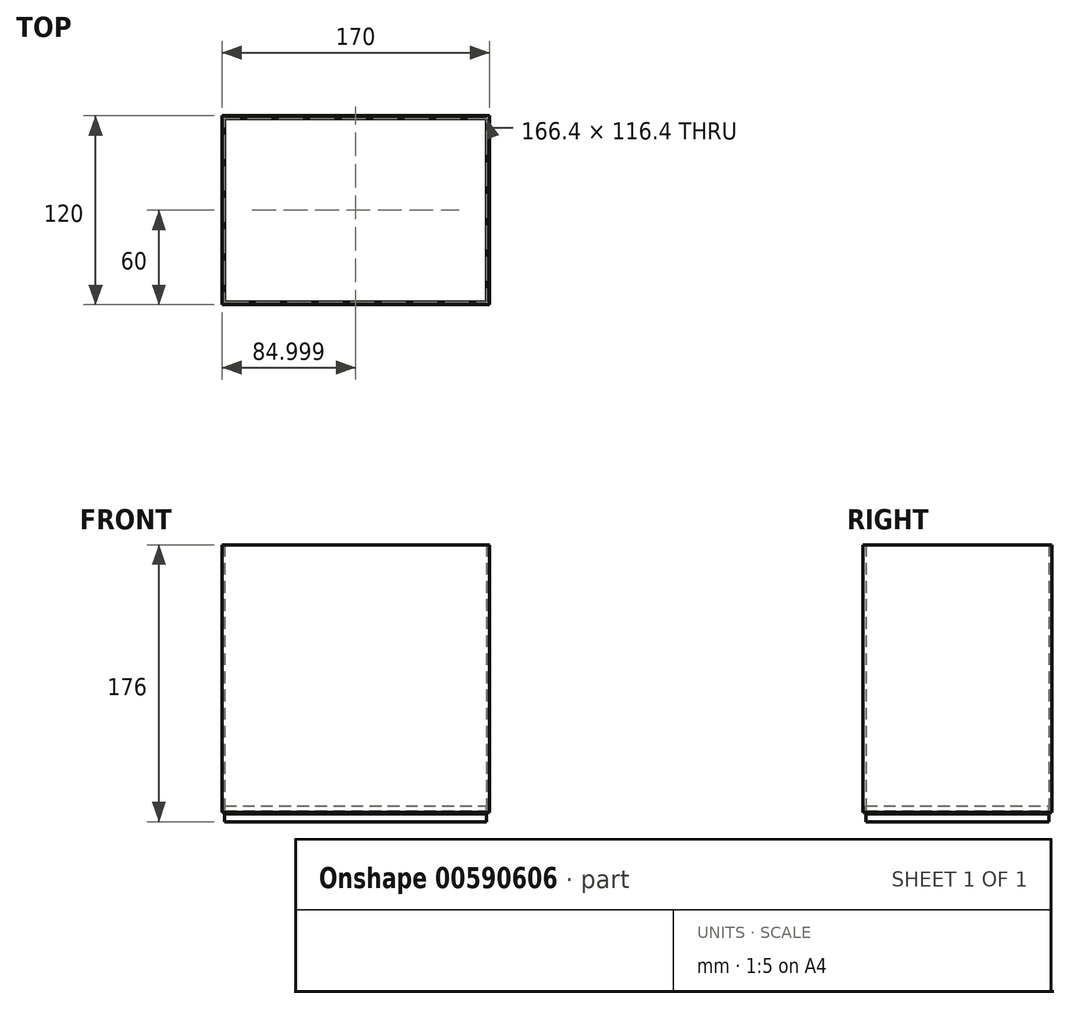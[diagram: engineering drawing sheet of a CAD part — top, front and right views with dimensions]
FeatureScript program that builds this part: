
annotation { "Feature Type Name" : "Feature", "Feature Type Description" : "" }
export const myFeature = defineFeature(function(context is Context, id is Id, definition is map)
    precondition{}
    {
        {
            var Q0;
            Q0=qCreatedBy(makeId("Top.planeOp"),FACE);
            var sketch = newSketch(context, id + "F0", { "sketchPlane" : qUnion([Q0])});
            skLineSegment(sketch, "E0.bottom", {"start": v(-78.22, 181.55) * mm, "end": v(91.78, 181.55) * mm});
            skLineSegment(sketch, "E0.top", {"start": v(-78.22, 61.55) * mm, "end": v(91.78, 61.55) * mm});
            skLineSegment(sketch, "E0.left", {"start": v(-78.22, 181.55) * mm, "end": v(-78.22, 61.55) * mm});
            skLineSegment(sketch, "E0.right", {"start": v(91.78, 181.55) * mm, "end": v(91.78, 61.55) * mm});
            skLineSegment(sketch, "E1.bottom", {"start": v(-76.42, 179.75) * mm, "end": v(89.98, 179.75) * mm});
            skLineSegment(sketch, "E1.top", {"start": v(-76.42, 63.35) * mm, "end": v(89.98, 63.35) * mm});
            skLineSegment(sketch, "E1.left", {"start": v(-76.42, 179.75) * mm, "end": v(-76.42, 63.35) * mm});
            skLineSegment(sketch, "E1.right", {"start": v(89.98, 179.75) * mm, "end": v(89.98, 63.35) * mm});
            skLineSegment(sketch, "E2.bottom", {"start": v(-76.42, -118.2) * mm, "end": v(93.58, -118.2) * mm});
            skLineSegment(sketch, "E2.top", {"start": v(-76.42, 1.8) * mm, "end": v(93.58, 1.8) * mm});
            skLineSegment(sketch, "E2.left", {"start": v(-76.42, -118.2) * mm, "end": v(-76.42, 1.8) * mm});
            skLineSegment(sketch, "E2.right", {"start": v(93.58, -118.2) * mm, "end": v(93.58, 1.8) * mm});
            skLineSegment(sketch, "E3.bottom", {"start": v(-74.62, -116.4) * mm, "end": v(91.78, -116.4) * mm});
            skLineSegment(sketch, "E3.top", {"start": v(-74.62, 0) * mm, "end": v(91.78, 0) * mm});
            skLineSegment(sketch, "E3.left", {"start": v(-74.62, -116.4) * mm, "end": v(-74.62, 0) * mm});
            skLineSegment(sketch, "E3.right", {"start": v(91.78, -116.4) * mm, "end": v(91.78, 0) * mm});
            skSolve(sketch);
        }
        {
            var Q0;
            Q0=makeQuery(id+"F0.imprint","IMPRINT",FACE,{"disambiguationData":[TD([[makeQuery(id+"F0.imprint","IMPRINT",EDGE,{"derivedFrom":sQuery(id+"F0.wireOp",EDGE,"E1.bottom")}),-1.0]])]});
            extrude(context, id + "F1", {"entities" : qUnion([Q0]), "depth" : 170 * mm, "offsetDistance" : 25 * mm});
        }
        {
            var Q0;
            Q0=makeQuery(id+"F0.imprint","IMPRINT",FACE,{"disambiguationData":[TD([[makeQuery(id+"F0.imprint","IMPRINT",EDGE,{"derivedFrom":sQuery(id+"F0.wireOp",EDGE,"E0.bottom")}),-1.0]])]});
            extrude(context, id + "F2", {"entities" : qUnion([Q0]), "depth" : 170 * mm, "offsetDistance" : 25 * mm});
        }
        {
            var Q0;
            Q0=makeQuery(id+"F1.opExtrude","SWEPT_BODY",BODY,{"disambiguationData":[OSD([sQuery(id+"F0.wireOp",EDGE,"E1.bottom"),sQuery(id+"F0.wireOp",EDGE,"E1.top"),sQuery(id+"F0.wireOp",EDGE,"E1.left"),sQuery(id+"F0.wireOp",EDGE,"E1.right")])]});
            var Q1;
            Q1=makeQuery(id+"F2.opExtrude","SWEPT_BODY",BODY,{"disambiguationData":[OSD([sQuery(id+"F0.wireOp",EDGE,"E0.bottom"),sQuery(id+"F0.wireOp",EDGE,"E0.top"),sQuery(id+"F0.wireOp",EDGE,"E0.left"),sQuery(id+"F0.wireOp",EDGE,"E0.right"),sQuery(id+"F0.wireOp",EDGE,"E1.bottom"),sQuery(id+"F0.wireOp",EDGE,"E1.top"),sQuery(id+"F0.wireOp",EDGE,"E1.left"),sQuery(id+"F0.wireOp",EDGE,"E1.right")])]});
            booleanBodies(context, id + "F3", {"operationType" : BooleanOperationType.SUBTRACTION, "tools" : qUnion([Q0]), "targets" : qUnion([Q1])});
        }
        {
            var Q0;
            Q0=makeQuery(id+"F0.imprint","IMPRINT",FACE,{"disambiguationData":[TD([[makeQuery(id+"F0.imprint","IMPRINT",EDGE,{"derivedFrom":sQuery(id+"F0.wireOp",EDGE,"E3.bottom")}),1.0]])]});
            extrude(context, id + "F4", {"entities" : qUnion([Q0]), "endBound" : BoundingType.SYMMETRIC, "depth" : 2 * mm, "offsetDistance" : 25 * mm});
        }
        {
            var Q0;
            Q0=makeQuery(id+"F4.opExtrude","CAP_FACE",FACE,{"disambiguationData":[OSD([sQuery(id+"F0.wireOp",EDGE,"E3.bottom"),sQuery(id+"F0.wireOp",EDGE,"E3.top"),sQuery(id+"F0.wireOp",EDGE,"E3.left"),sQuery(id+"F0.wireOp",EDGE,"E3.right")])],"isStart":true});
            extrude(context, id + "F5", {"entities" : qUnion([Q0]), "endBound" : BoundingType.SYMMETRIC, "depth" : 10 * mm, "offsetDistance" : 25 * mm});
        }
        {
            var Q0;
            Q0=makeQuery(id+"F0.imprint","IMPRINT",FACE,{"disambiguationData":[TD([[makeQuery(id+"F0.imprint","IMPRINT",EDGE,{"derivedFrom":sQuery(id+"F0.wireOp",EDGE,"E2.bottom")}),1.0]])]});
            extrude(context, id + "F6", {"entities" : qUnion([Q0]), "depth" : 170 * mm, "offsetDistance" : 25 * mm});
        }
        {
            var Q0;
            Q0=makeQuery(id+"F2.opExtrude","SWEPT_BODY",BODY,{"disambiguationData":[OSD([sQuery(id+"F0.wireOp",EDGE,"E0.bottom"),sQuery(id+"F0.wireOp",EDGE,"E0.top"),sQuery(id+"F0.wireOp",EDGE,"E0.left"),sQuery(id+"F0.wireOp",EDGE,"E0.right"),sQuery(id+"F0.wireOp",EDGE,"E1.bottom"),sQuery(id+"F0.wireOp",EDGE,"E1.top"),sQuery(id+"F0.wireOp",EDGE,"E1.left"),sQuery(id+"F0.wireOp",EDGE,"E1.right")])]});
            deleteBodies(context, id + "F7", {"entities" : qUnion([Q0])});
        }
    });
